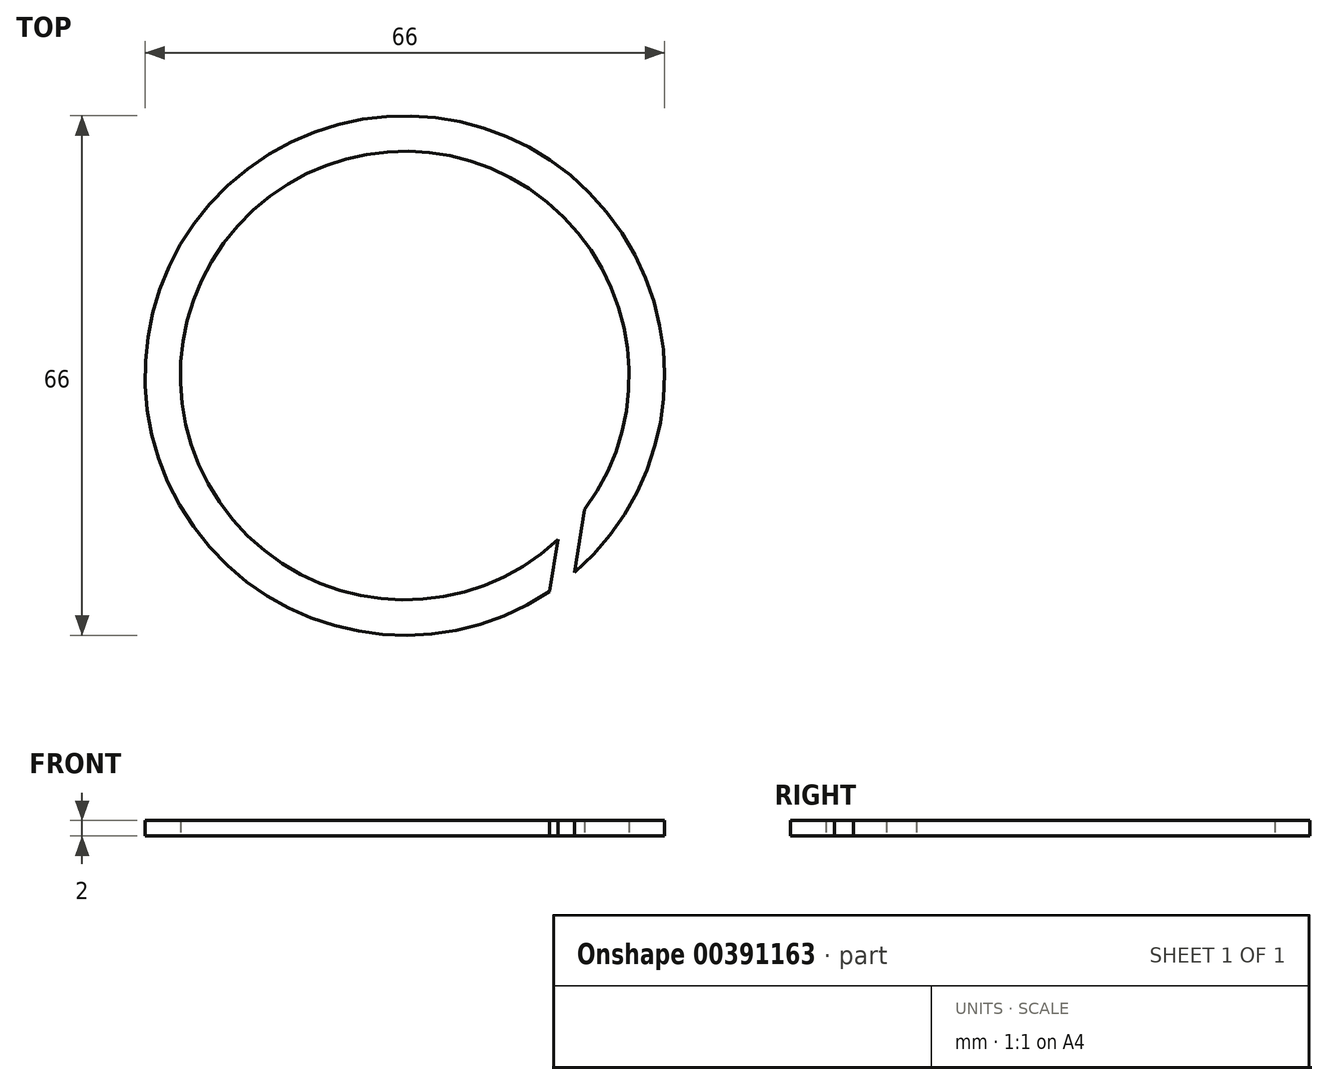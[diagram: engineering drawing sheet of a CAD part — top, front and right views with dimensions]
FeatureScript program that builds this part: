
annotation { "Feature Type Name" : "Feature", "Feature Type Description" : "" }
export const myFeature = defineFeature(function(context is Context, id is Id, definition is map)
    precondition{}
    {
        {
            var Q0;
            Q0=qCreatedBy(makeId("Top.planeOp"),FACE);
            var sketch = newSketch(context, id + "F0", { "sketchPlane" : qUnion([Q0])});
            skCircle(sketch, "E0", {"center": v(0, 0) * mm, "radius": 33 * mm});
            skCircle(sketch, "E1", {"center": v(0, 0) * mm, "radius": 28.5 * mm});
            skLineSegment(sketch, "E2", {"start": v(19.44, -20.84) * mm, "end": v(18.37, -27.41) * mm});
            skLineSegment(sketch, "E3", {"start": v(22.85, -17.03) * mm, "end": v(21.55, -25) * mm});
            skSolve(sketch);
        }
        {
            var Q0;
            {var subQ0=sQuery(id+"F0.wireOp",EDGE,"E2");Q0=makeQuery(id+"F0.imprint","IMPRINT",FACE,{"disambiguationData":[TD([[makeQuery(id+"F0.imprint","IMPRINT",EDGE,{"derivedFrom":subQ0}),-1.0]])]});}
            extrude(context, id + "F1", {"entities" : qUnion([Q0]), "depth" : 2 * mm, "offsetDistance" : 25 * mm});
        }
    });
